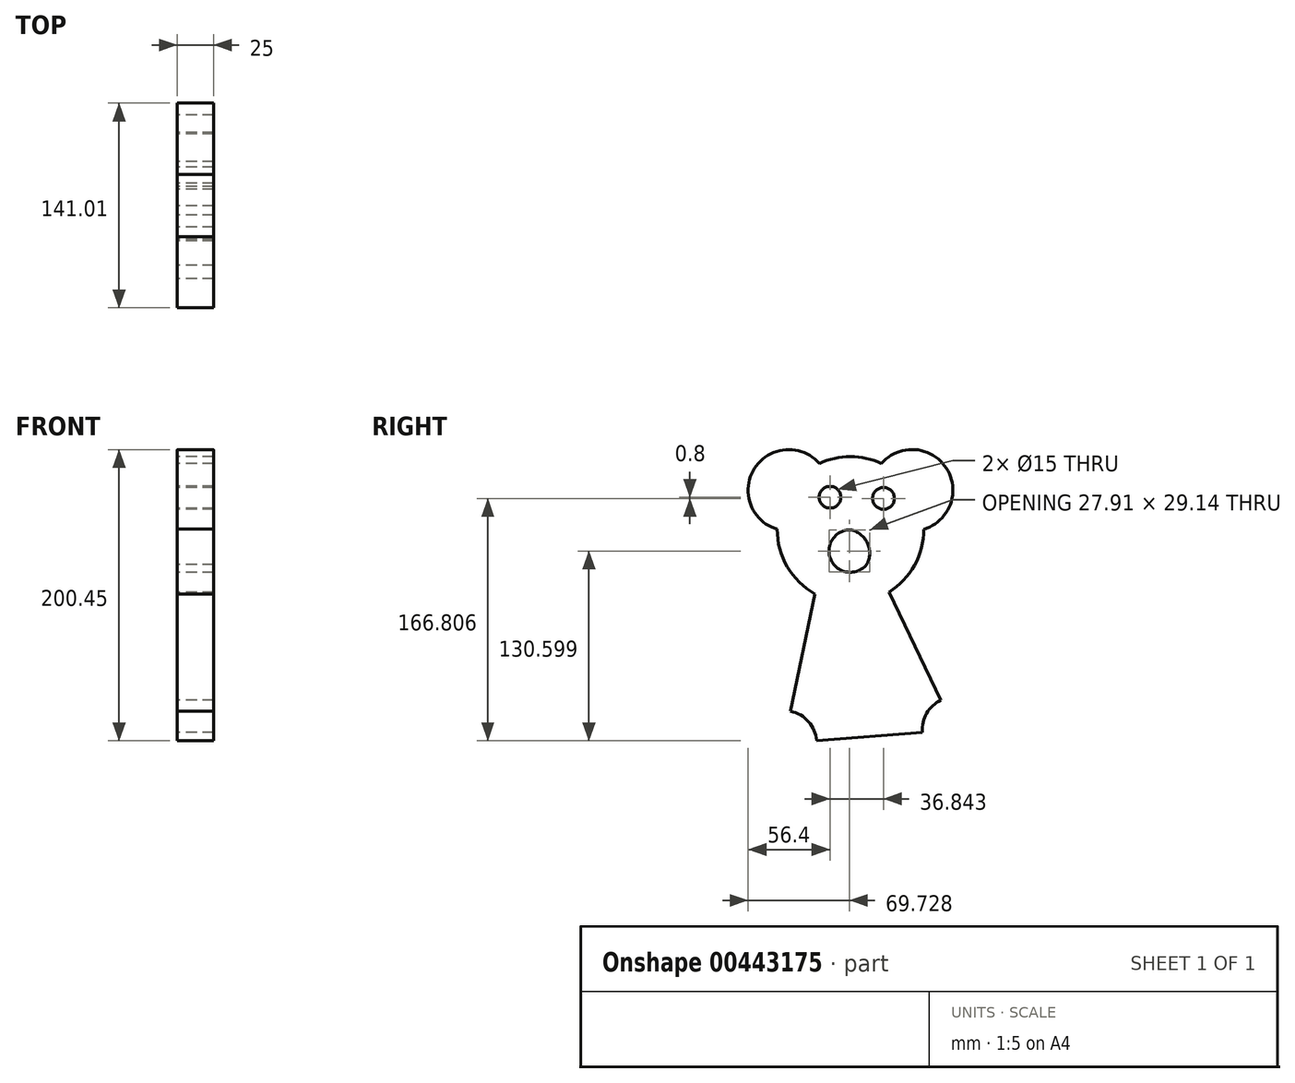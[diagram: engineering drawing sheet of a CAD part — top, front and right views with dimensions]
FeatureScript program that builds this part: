
annotation { "Feature Type Name" : "Feature", "Feature Type Description" : "" }
export const myFeature = defineFeature(function(context is Context, id is Id, definition is map)
    precondition{}
    {
        {
            var Q0;
            Q0=qCreatedBy(makeId("Right.planeOp"),FACE);
            var sketch = newSketch(context, id + "F0", { "sketchPlane" : qUnion([Q0])});
            skCircle(sketch, "E0", {"center": v(0, 0) * mm, "radius": 50.45 * mm});
            skArc(sketch, "E1", {"start": v(50.44, 0.31) * mm, "mid": v(66.1, 42.36) * mm, "end": v(21.36, 45.7) * mm});
            skPoint(sketch, "E2.center.orphan", {"position": v(-50.45, 0) * mm});
            skCircle(sketch, "E3", {"center": v(-14.07, 22.44) * mm, "radius": 7.5 * mm});
            skArc(sketch, "E4", {"start": v(0, 0) * mm, "mid": v(-13.37, -20.8) * mm, "end": v(11.14, -24) * mm});
            skArc(sketch, "E5", {"start": v(11.14, -24) * mm, "mid": v(11.7, -9.15) * mm, "end": v(0, 0) * mm});
            skLineSegment(sketch, "E6", {"start": v(26.51, -42.92) * mm, "end": v(72.02, -137.54) * mm});
            skLineSegment(sketch, "E7", {"start": v(-24.36, -44.18) * mm, "end": v(-45.78, -146.97) * mm});
            skCircle(sketch, "E8", {"center": v(72.02, -137.54) * mm, "radius": 22.5 * mm});
            skCircle(sketch, "E9", {"center": v(-45.78, -146.97) * mm, "radius": 22.5 * mm});
            skLineSegment(sketch, "E10", {"start": v(72.02, -137.54) * mm, "end": v(-45.78, -146.97) * mm});
            skCircle(sketch, "E11", {"center": v(22.77, 21.64) * mm, "radius": 7.5 * mm});
            skLineSegment(sketch, "E12", {"start": v(42.47, 27.22) * mm, "end": v(-42.47, 27.22) * mm});
            skArc(sketch, "E13", {"start": v(-14.47, 27.22) * mm, "mid": v(-14.5, 28.57) * mm, "end": v(-14.6, 29.92) * mm});
            skArc(sketch, "E14.trimOffspring", {"start": v(-21.42, 45.67) * mm, "mid": v(-66.05, 42.33) * mm, "end": v(-50.44, 0.38) * mm});
            skSolve(sketch);
        }
        {
            var Q0;
            {var subQ1=sQuery(id+"F0.wireOp",EDGE,"E6");var subQ5=sQuery(id+"F0.wireOp",EDGE,"E0");var subQ6=makeQuery(id+"F0.imprint","INTERSECT",VERTEX,{"derivedFrom":[subQ5,subQ1]});Q0=makeQuery(id+"F0.imprint","IMPRINT",FACE,{"disambiguationData":[TD([[makeQuery(id+"F0.imprint","IMPRINT",EDGE,{"disambiguationData":[TD([[subQ6,1.0]])],"derivedFrom":subQ5}),-1.0]])]});}
            var Q1;
            Q1=makeQuery(id+"F0.imprint","IMPRINT",FACE,{"disambiguationData":[TD([[makeQuery(id+"F0.imprint","IMPRINT",EDGE,{"derivedFrom":sQuery(id+"F0.wireOp",EDGE,"E4")}),-1.0]])]});
            var Q2;
            {var subQ4=sQuery(id+"F0.wireOp",EDGE,"E0");var subQ10=makeQuery(id+"F0.imprint","INTERSECT",VERTEX,{"disambiguationData":[OD(1.0)],"derivedFrom":[subQ4,sQuery(id+"F0.wireOp",EDGE,"E1")]});Q2=makeQuery(id+"F0.imprint","IMPRINT",FACE,{"disambiguationData":[TD([[makeQuery(id+"F0.imprint","IMPRINT",EDGE,{"disambiguationData":[TD([[subQ10,1.0]])],"derivedFrom":subQ4}),1.0]])]});}
            var Q3;
            {var subQ2=sQuery(id+"F0.wireOp",EDGE,"E14.trimOffspring");Q3=makeQuery(id+"F0.imprint","IMPRINT",FACE,{"disambiguationData":[TD([[makeQuery(id+"F0.imprint","IMPRINT",EDGE,{"derivedFrom":subQ2}),1.0]])]});}
            var Q4;
            {var subQ0=sQuery(id+"F0.wireOp",EDGE,"E1");Q4=makeQuery(id+"F0.imprint","IMPRINT",FACE,{"disambiguationData":[TD([[makeQuery(id+"F0.imprint","IMPRINT",EDGE,{"derivedFrom":subQ0}),1.0]])]});}
            extrude(context, id + "F1", {"entities" : qUnion([Q0, Q1, Q2, Q3, Q4]), "depth" : 25 * mm});
        }
    });
